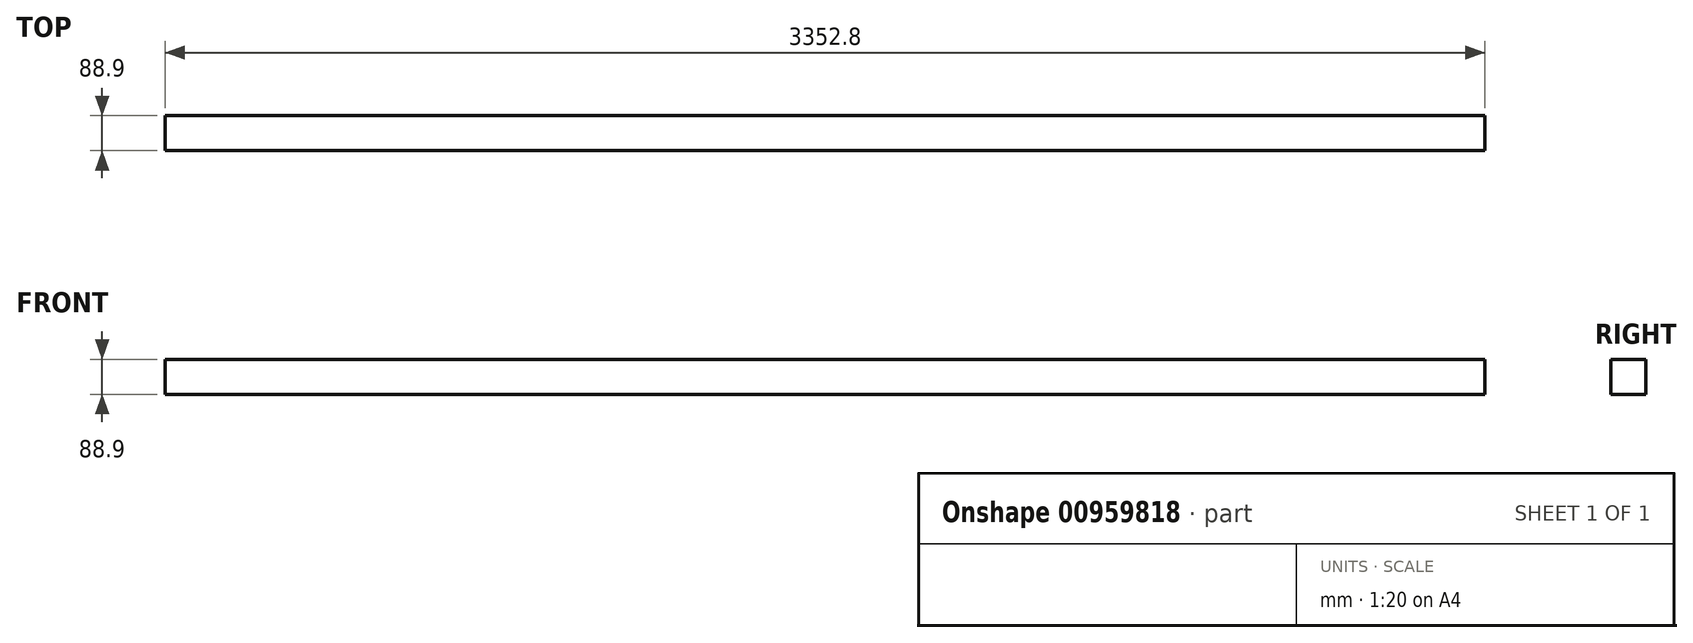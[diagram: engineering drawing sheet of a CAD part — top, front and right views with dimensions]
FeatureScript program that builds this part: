
annotation { "Feature Type Name" : "Feature", "Feature Type Description" : "" }
export const myFeature = defineFeature(function(context is Context, id is Id, definition is map)
    precondition{}
    {
        {
            var Q0;
            Q0=qCreatedBy(makeId("Right.planeOp"),FACE);
            var sketch = newSketch(context, id + "F0", { "sketchPlane" : qUnion([Q0])});
            skLineSegment(sketch, "E0.bottom", {"start": v(44.45, 44.45) * mm, "end": v(-44.45, 44.45) * mm});
            skLineSegment(sketch, "E0.top", {"start": v(44.45, -44.45) * mm, "end": v(-44.45, -44.45) * mm});
            skLineSegment(sketch, "E0.left", {"start": v(44.45, 44.45) * mm, "end": v(44.45, -44.45) * mm});
            skLineSegment(sketch, "E0.right", {"start": v(-44.45, 44.45) * mm, "end": v(-44.45, -44.45) * mm});
            skPoint(sketch, "E0.middle", {"position": v(0, 0) * mm});
            skSolve(sketch);
        }
        {
            var Q0;
            Q0=makeQuery(id+"F0.imprint","IMPRINT",FACE,{"disambiguationData":[TD([[makeQuery(id+"F0.imprint","IMPRINT",EDGE,{"derivedFrom":sQuery(id+"F0.wireOp",EDGE,"E0.bottom")}),1.0]])]});
            extrude(context, id + "F1", {"entities" : qUnion([Q0]), "endBound" : BoundingType.SYMMETRIC, "depth" : 3352.8 * mm, "offsetDistance" : 25.4 * mm});
        }
    });
